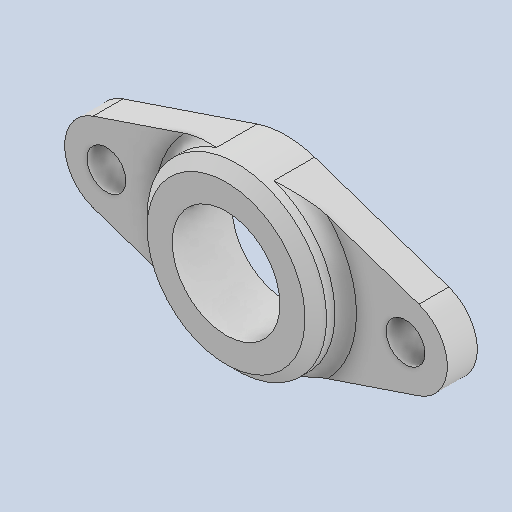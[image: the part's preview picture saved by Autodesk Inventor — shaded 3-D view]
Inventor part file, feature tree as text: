
AUTODESK INVENTOR PART (.ipt)
format: ipt  version: 2023 (Build 270158000, 158)  size: 144,384 bytes
history: native  units: in
note: dims shown in document units (in); Inventor stores cm internally (conversion verified against a paired STEP export)
features: fillet x1
ambient origin geometry x8: Origin, YZ Plane, XZ Plane, XY Plane, X Axis, Y Axis, Z Axis, Center Point
bodies: Solid1 (feature_tree)
feature tree (1):
  fillet  "Fillet1"  [1 undecoded]
note: 1 required parameter value undecoded (feature->parameter linkage not recoverable at this tier; creation-order binding heuristic only, values carry confidence <= 0.55)
